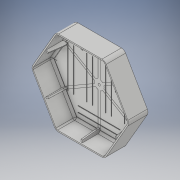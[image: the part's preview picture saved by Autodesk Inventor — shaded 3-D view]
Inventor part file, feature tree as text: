
AUTODESK INVENTOR PART (.ipt)
format: ipt  version: 2019 (Build 230136000, 136)  size: 922,112 bytes
history: native  units: mm
features: projected_geometry x23, sketch x9, extrude x5, plane x3, fillet x3, other x3, shell x1, pattern_circular x1
ambient origin geometry x8: Origin, YZ Plane, XZ Plane, XY Plane, X Axis, Y Axis, Z Axis, Center Point
bodies: Solid1 (feature_tree)
feature tree (48):
  extrude  "Extrusion1"  Depth=40.0mm TaperAngle=0.0deg
  shell  "Shell1"  Thickness=2.5mm
  extrude  "Extrusion9"  Depth=10.0mm
  plane  "Work Plane1"
  plane  "Work Plane2"
  plane  "Work Plane3"
  sketch  "Sketch12"  dims[d55=5.0mm]
  extrude  "Extrusion5"  Depth=5.0mm
  extrude  "Extrusion6"  TaperAngle=60.0deg  [1 undecoded]
  extrude  "Extrusion8"  TaperAngle=90.0deg  [1 undecoded]
  pattern_circular  "Circular Pattern1"  [2 undecoded]
  fillet  "Fillet1"  Radius=8.0mm
  fillet  "Fillet2"  Radius=36.0mm
  fillet  "Fillet4"  Radius=60.0mm
  sketch  "Sketch5"  dims[d12=1.0mm d37=5.0mm]
  sketch  "Sketch6"  dims[d44=10.0mm d45=60.0deg]
  sketch  "Sketch7"  dims[d46=90.0deg d47=90.0deg]
  other  "Work Axis4"
  other  "Work Axis5"
  other  "Work Axis6"
  sketch  "Sketch13"  dims[d56=2.0mm d57=3.0mm d58=8.0mm d59=36.0mm d60=0.0mm d70=60.0mm d72=360.0deg d74=60.0mm d75=360.0deg d77=3.0mm d78=30.0mm d79=20.0mm d80=0.0mm d147=130.0mm d149=0.5mm d150=0.0mm d151=1.0mm d156=1.0mm d157=11.0mm d158=87.0mm d167=117.0mm d168=1.0mm d169=87.0mm d170=1.0mm d171=87.0mm d172=40.0mm d174=39.0mm d175=10.0mm d177=10.0mm d179=1.0mm d180=1.0mm d181=3.0mm]
  sketch  "Sketch1"  dims[d0=175.0mm d2=40.0mm d3=0.0mm d4=2.5mm]
  sketch  "Sketch4"  dims[d10=4.0mm d11=10.0mm]
  projected_geometry  "Projected Loop3"
  sketch  "Sketch8"  dims[d52=5.5mm]
  projected_geometry  "Projected Loop4"
  sketch  "Sketch9"  dims[d53=0.01mm d54=0.0mm]
  projected_geometry  "Projected Loop5"
  projected_geometry  "Projected Loop6"
  projected_geometry  "Projected Loop7"
  projected_geometry  "Projected Loop8"
  projected_geometry  "Projected Loop9"
  projected_geometry  "Projected Loop10"
  projected_geometry  "Projected Loop11"
  projected_geometry  "Projected Loop12"
  projected_geometry  "Projected Loop13"
  projected_geometry  "Projected Loop14"
  projected_geometry  "Projected Loop15"
  projected_geometry  "Projected Loop16"
  projected_geometry  "Projected Loop17"
  projected_geometry  "Projected Loop18"
  projected_geometry  "Projected Loop19"
  projected_geometry  "Projected Loop20"
  projected_geometry  "Projected Loop21"
  projected_geometry  "Projected Loop22"
  projected_geometry  "Projected Loop23"
  projected_geometry  "Projected Loop24"
  projected_geometry  "Projected Loop25"
note: 4 required parameter values undecoded (feature->parameter linkage not recoverable at this tier; creation-order binding heuristic only, values carry confidence <= 0.55)
